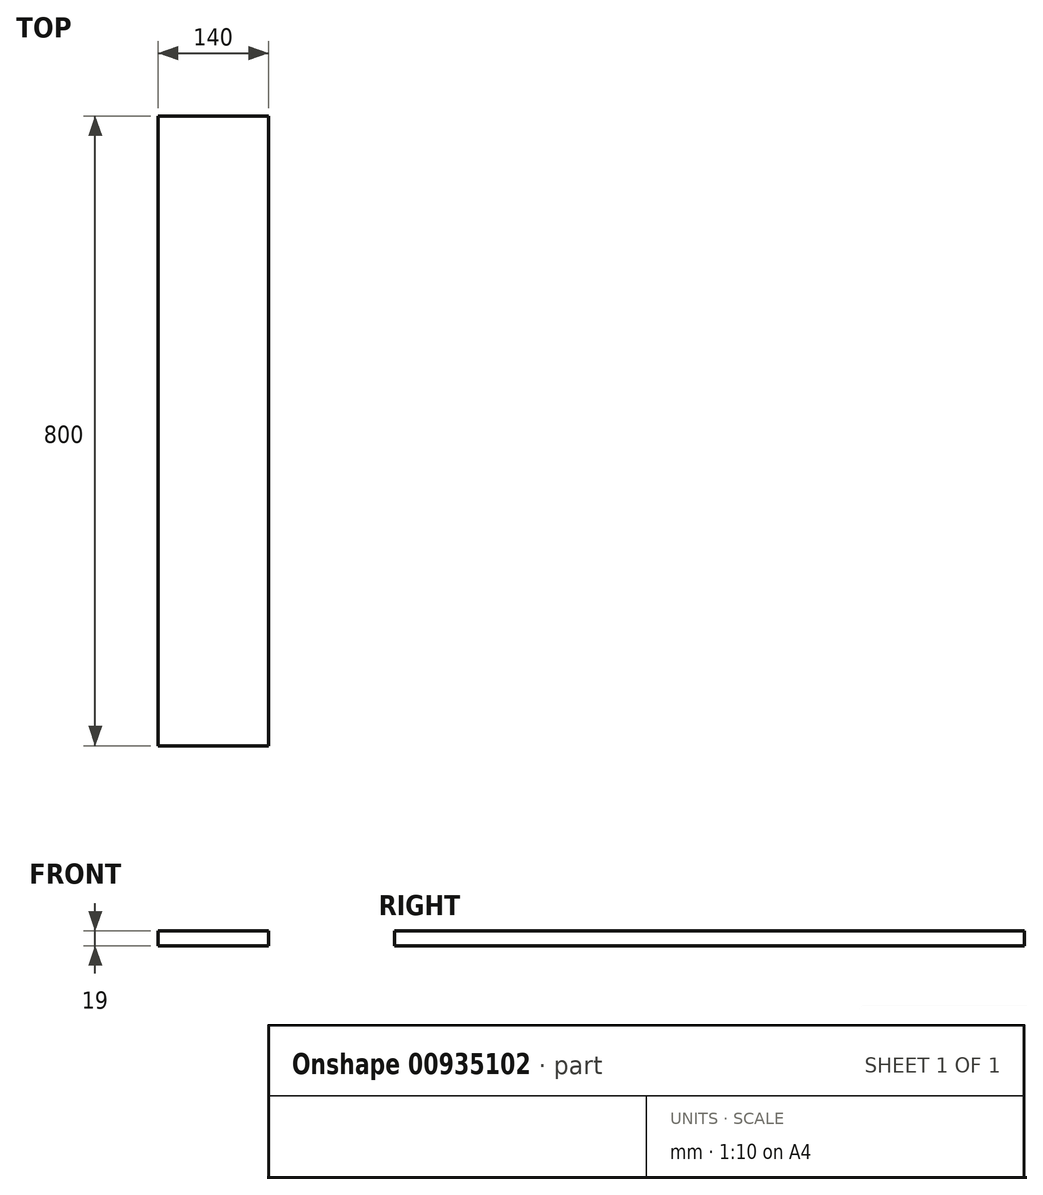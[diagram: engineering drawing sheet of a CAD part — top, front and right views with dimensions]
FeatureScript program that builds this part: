
annotation { "Feature Type Name" : "Feature", "Feature Type Description" : "" }
export const myFeature = defineFeature(function(context is Context, id is Id, definition is map)
    precondition{}
    {
        {
            var Q0;
            Q0=qCreatedBy(makeId("Front.planeOp"),FACE);
            var sketch = newSketch(context, id + "F0", { "sketchPlane" : qUnion([Q0])});
            skLineSegment(sketch, "E0.bottom", {"start": v(0, 0) * mm, "end": v(140, 0) * mm});
            skLineSegment(sketch, "E0.top", {"start": v(0, 19) * mm, "end": v(140, 19) * mm});
            skLineSegment(sketch, "E0.left", {"start": v(0, 0) * mm, "end": v(0, 19) * mm});
            skLineSegment(sketch, "E0.right", {"start": v(140, 0) * mm, "end": v(140, 19) * mm});
            skSolve(sketch);
        }
        {
            var Q0;
            Q0=makeQuery(id+"F0.imprint","IMPRINT",FACE,{"disambiguationData":[TD([[makeQuery(id+"F0.imprint","IMPRINT",EDGE,{"derivedFrom":sQuery(id+"F0.wireOp",EDGE,"E0.bottom")}),1.0]])]});
            extrude(context, id + "F1", {"entities" : qUnion([Q0]), "depth" : 800 * mm, "offsetDistance" : 25 * mm});
        }
    });
